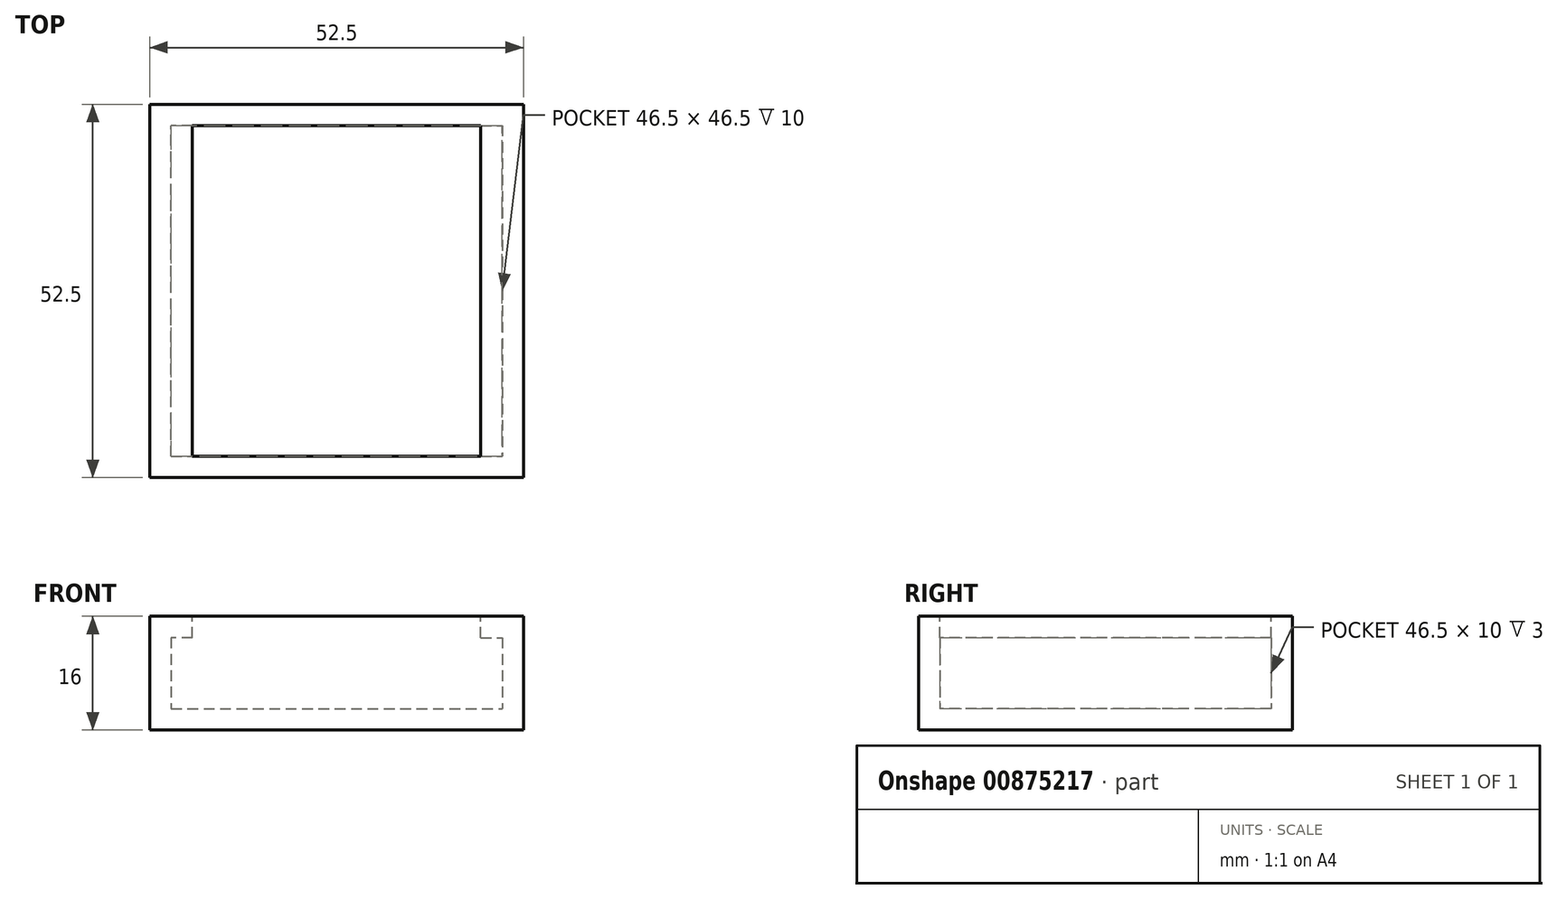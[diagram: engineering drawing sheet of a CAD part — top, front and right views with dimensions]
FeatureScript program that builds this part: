
annotation { "Feature Type Name" : "Feature", "Feature Type Description" : "" }
export const myFeature = defineFeature(function(context is Context, id is Id, definition is map)
    precondition{}
    {
        {
            var Q0;
            Q0=qCreatedBy(makeId("Top.planeOp"),FACE);
            var sketch = newSketch(context, id + "F0", { "sketchPlane" : qUnion([Q0])});
            skLineSegment(sketch, "E0.bottom", {"start": v(20.25, 20.25) * mm, "end": v(-20.25, 20.25) * mm, "construction": true});
            skLineSegment(sketch, "E0.top", {"start": v(20.25, -20.25) * mm, "end": v(-20.25, -20.25) * mm, "construction": true});
            skLineSegment(sketch, "E0.left", {"start": v(20.25, 20.25) * mm, "end": v(20.25, -20.25) * mm, "construction": true});
            skLineSegment(sketch, "E0.right", {"start": v(-20.25, 20.25) * mm, "end": v(-20.25, -20.25) * mm, "construction": true});
            skPoint(sketch, "E0.middle", {"position": v(0, 0) * mm});
            skLineSegment(sketch, "E1.bottom", {"start": v(-23.25, 23.25) * mm, "end": v(23.25, 23.25) * mm, "construction": true});
            skLineSegment(sketch, "E1.top", {"start": v(-23.25, -23.25) * mm, "end": v(23.25, -23.25) * mm, "construction": true});
            skLineSegment(sketch, "E1.left", {"start": v(-23.25, 23.25) * mm, "end": v(-23.25, -23.25) * mm, "construction": true});
            skLineSegment(sketch, "E1.right", {"start": v(23.25, 23.25) * mm, "end": v(23.25, -23.25) * mm, "construction": true});
            skLineSegment(sketch, "E2.bottom", {"start": v(-26.25, 26.25) * mm, "end": v(26.25, 26.25) * mm});
            skLineSegment(sketch, "E2.top", {"start": v(-26.25, -26.25) * mm, "end": v(26.25, -26.25) * mm});
            skLineSegment(sketch, "E2.left", {"start": v(-26.25, 26.25) * mm, "end": v(-26.25, -26.25) * mm});
            skLineSegment(sketch, "E2.right", {"start": v(26.25, 26.25) * mm, "end": v(26.25, -26.25) * mm});
            skSolve(sketch);
        }
        {
            var Q0;
            Q0=makeQuery(id+"F0.imprint","IMPRINT",FACE,{"disambiguationData":[TD([[makeQuery(id+"F0.imprint","IMPRINT",EDGE,{"derivedFrom":sQuery(id+"F0.wireOp",EDGE,"E2.bottom")}),-1.0]])]});
            extrude(context, id + "F1", {"entities" : qUnion([Q0]), "depth" : 3 * mm, "offsetDistance" : 25 * mm});
        }
        {
            var Q0;
            Q0=makeQuery(id+"F1.opExtrude","CAP_FACE",FACE,{"disambiguationData":[OSD([sQuery(id+"F0.wireOp",EDGE,"E2.bottom"),sQuery(id+"F0.wireOp",EDGE,"E2.top"),sQuery(id+"F0.wireOp",EDGE,"E2.left"),sQuery(id+"F0.wireOp",EDGE,"E2.right")])],"isStart":false});
            var sketch = newSketch(context, id + "F2", { "sketchPlane" : qUnion([Q0])});
            skLineSegment(sketch, "E3.bottom", {"start": v(-23.25, 23.25) * mm, "end": v(23.25, 23.25) * mm});
            skLineSegment(sketch, "E3.top", {"start": v(-23.25, -23.25) * mm, "end": v(23.25, -23.25) * mm});
            skLineSegment(sketch, "E3.left", {"start": v(-23.25, 23.25) * mm, "end": v(-23.25, -23.25) * mm});
            skLineSegment(sketch, "E3.right", {"start": v(23.25, 23.25) * mm, "end": v(23.25, -23.25) * mm});
            skPoint(sketch, "E3.middle", {"position": v(0, 0) * mm});
            skSolve(sketch);
        }
        {
            var Q0;
            Q0=makeQuery(id+"F2.imprint","IMPRINT",FACE,{"disambiguationData":[TD([[makeQuery(id+"F2.imprint","IMPRINT",EDGE,{"derivedFrom":sQuery(id+"F2.wireOp",EDGE,"E3.bottom")}),1.0]])]});
            extrude(context, id + "F3", {"entities" : qUnion([Q0]), "operationType" : NewBodyOperationType.ADD, "depth" : 13 * mm, "offsetDistance" : 25 * mm});
        }
        {
            var Q0;
            {var subQ0=sQuery(id+"F0.wireOp",EDGE,"E2.top");Q0=makeQuery(id+"F3.boolean.opBoolean","MERGE",FACE,{"derivedFrom":[makeQuery(id+"F1.opExtrude","SWEPT_FACE",FACE,{"disambiguationData":[OSD([subQ0])]}),makeQuery(id+"F3.opExtrude","SWEPT_FACE",FACE,{"disambiguationData":[OSD([subQ0])]})]});}
            var sketch = newSketch(context, id + "F4", { "sketchPlane" : qUnion([Q0])});
            skLineSegment(sketch, "E4.bottom", {"start": v(-26.25, 16) * mm, "end": v(-20.25, 16) * mm});
            skLineSegment(sketch, "E4.top", {"start": v(-26.25, 13) * mm, "end": v(-20.25, 13) * mm});
            skLineSegment(sketch, "E4.left", {"start": v(-26.25, 16) * mm, "end": v(-26.25, 13) * mm});
            skLineSegment(sketch, "E4.right", {"start": v(-20.25, 16) * mm, "end": v(-20.25, 13) * mm});
            skLineSegment(sketch, "E5.bottom", {"start": v(26.25, 16) * mm, "end": v(20.25, 16) * mm});
            skLineSegment(sketch, "E5.top", {"start": v(26.25, 13) * mm, "end": v(20.25, 13) * mm});
            skLineSegment(sketch, "E5.left", {"start": v(26.25, 16) * mm, "end": v(26.25, 13) * mm});
            skLineSegment(sketch, "E5.right", {"start": v(20.25, 16) * mm, "end": v(20.25, 13) * mm});
            skSolve(sketch);
        }
        {
            var Q0;
            Q0=makeQuery(id+"F4.imprint","IMPRINT",FACE,{"disambiguationData":[TD([[makeQuery(id+"F4.imprint","IMPRINT",EDGE,{"derivedFrom":sQuery(id+"F4.wireOp",EDGE,"E4.bottom")}),-1.0]])]});
            var Q1;
            Q1=makeQuery(id+"F4.imprint","IMPRINT",FACE,{"disambiguationData":[TD([[makeQuery(id+"F4.imprint","IMPRINT",EDGE,{"derivedFrom":sQuery(id+"F4.wireOp",EDGE,"E5.bottom")}),-1.0]])]});
            extrude(context, id + "F5", {"entities" : qUnion([Q0, Q1]), "operationType" : NewBodyOperationType.ADD, "oppositeDirection" : true, "depth" : 52.5 * mm, "offsetDistance" : 25 * mm});
        }
    });
